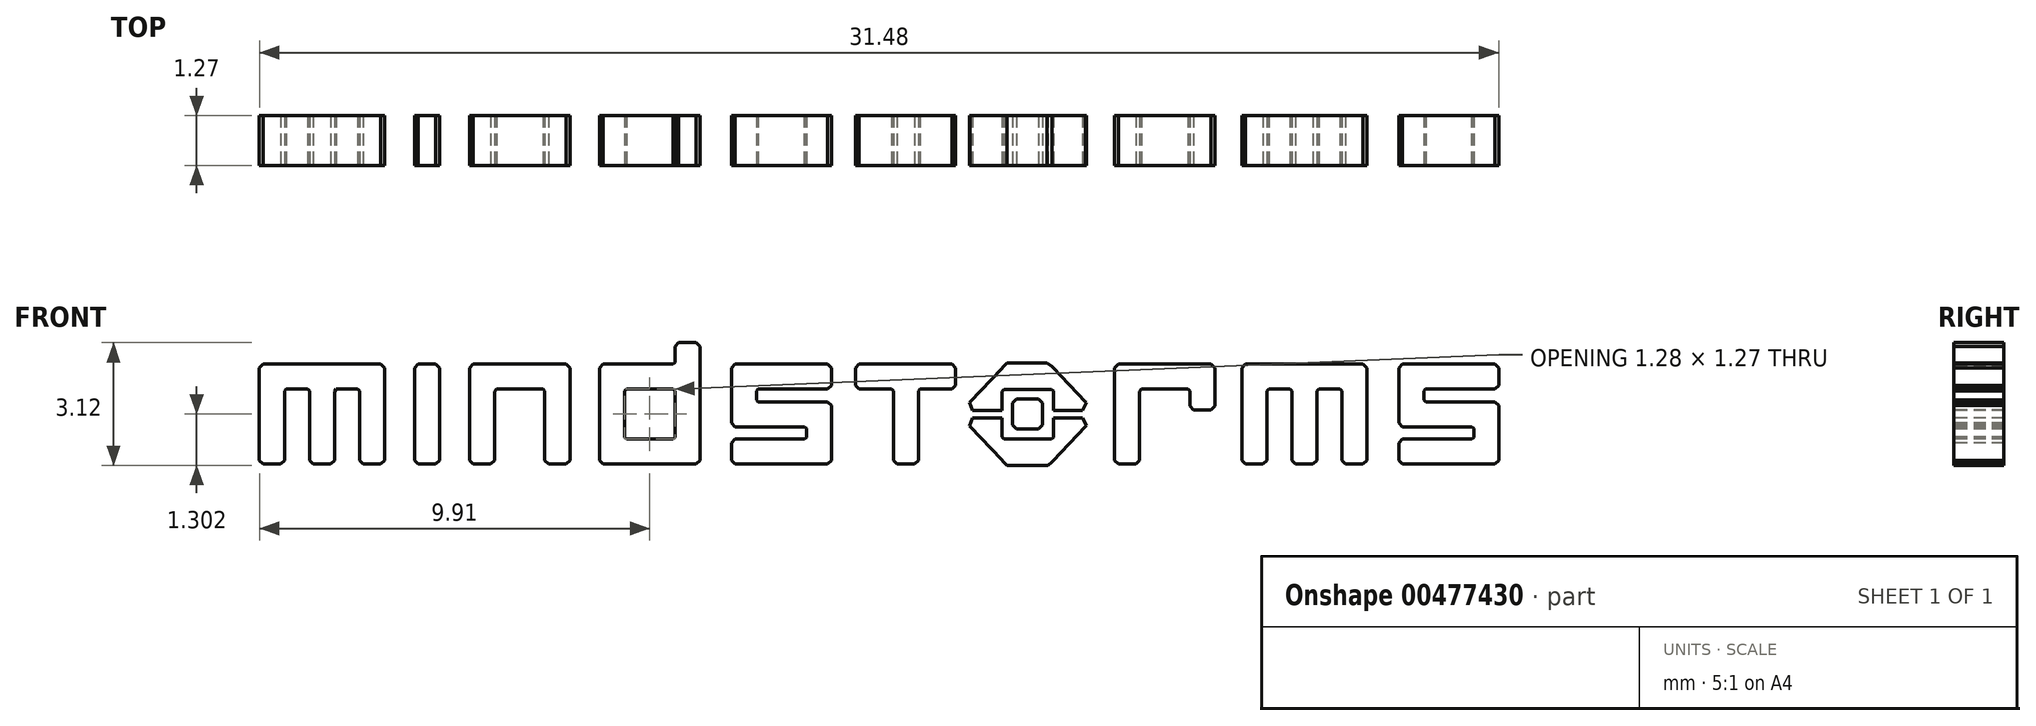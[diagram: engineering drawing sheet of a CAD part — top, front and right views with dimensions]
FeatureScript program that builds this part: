
annotation { "Feature Type Name" : "Feature", "Feature Type Description" : "" }
export const myFeature = defineFeature(function(context is Context, id is Id, definition is map)
    precondition{}
    {
        {
            var Q0;
            Q0=qCreatedBy(makeId("Front.planeOp"),FACE);
            var sketch = newSketch(context, id + "F0", { "sketchPlane" : qUnion([Q0])});
            skLineSegment(sketch, "E0", {"start": v(4.43, -0.35) * mm, "end": v(5.14, -0.35) * mm});
            skLineSegment(sketch, "E1", {"start": v(5.14, -0.35) * mm, "end": v(5.17, -0.35) * mm});
            skLineSegment(sketch, "E2", {"start": v(5.17, -0.35) * mm, "end": v(5.26, -0.55) * mm});
            skLineSegment(sketch, "E3", {"start": v(5.26, -0.55) * mm, "end": v(5.25, -0.57) * mm});
            skLineSegment(sketch, "E4", {"start": v(5.25, -0.57) * mm, "end": v(4.42, -1.44) * mm});
            skLineSegment(sketch, "E5", {"start": v(4.42, -1.44) * mm, "end": v(4.38, -1.47) * mm});
            skLineSegment(sketch, "E6", {"start": v(4.38, -1.47) * mm, "end": v(4.29, -1.56) * mm});
            skLineSegment(sketch, "E7", {"start": v(4.29, -1.56) * mm, "end": v(4.25, -1.56) * mm});
            skLineSegment(sketch, "E8", {"start": v(4.25, -1.56) * mm, "end": v(3.3, -1.56) * mm});
            skLineSegment(sketch, "E9", {"start": v(3.3, -1.56) * mm, "end": v(3.25, -1.56) * mm});
            skLineSegment(sketch, "E10", {"start": v(3.25, -1.56) * mm, "end": v(3.15, -1.46) * mm});
            skLineSegment(sketch, "E11", {"start": v(3.15, -1.46) * mm, "end": v(3.11, -1.42) * mm});
            skLineSegment(sketch, "E12", {"start": v(3.11, -1.42) * mm, "end": v(2.3, -0.57) * mm});
            skLineSegment(sketch, "E13", {"start": v(2.3, -0.57) * mm, "end": v(2.3, -0.55) * mm});
            skLineSegment(sketch, "E14", {"start": v(2.3, -0.55) * mm, "end": v(2.38, -0.35) * mm});
            skLineSegment(sketch, "E15", {"start": v(2.38, -0.35) * mm, "end": v(2.4, -0.35) * mm});
            skLineSegment(sketch, "E16", {"start": v(2.4, -0.35) * mm, "end": v(3.12, -0.35) * mm});
            skLineSegment(sketch, "E17", {"start": v(3.12, -0.35) * mm, "end": v(3.12, -0.83) * mm});
            skLineSegment(sketch, "E18", {"start": v(3.12, -0.83) * mm, "end": v(3.12, -0.84) * mm});
            skLineSegment(sketch, "E19", {"start": v(3.12, -0.84) * mm, "end": v(3.17, -0.9) * mm});
            skLineSegment(sketch, "E20", {"start": v(3.17, -0.9) * mm, "end": v(3.18, -0.9) * mm});
            skLineSegment(sketch, "E21", {"start": v(3.18, -0.9) * mm, "end": v(4.36, -0.9) * mm});
            skLineSegment(sketch, "E22", {"start": v(4.36, -0.9) * mm, "end": v(4.38, -0.9) * mm});
            skLineSegment(sketch, "E23", {"start": v(4.38, -0.9) * mm, "end": v(4.43, -0.84) * mm});
            skLineSegment(sketch, "E24", {"start": v(4.43, -0.84) * mm, "end": v(4.43, -0.83) * mm});
            skLineSegment(sketch, "E25", {"start": v(4.43, -0.83) * mm, "end": v(4.43, -0.35) * mm});
            skLineSegment(sketch, "E26", {"start": v(4.43, -0.16) * mm, "end": v(5.14, -0.16) * mm});
            skLineSegment(sketch, "E27", {"start": v(5.14, -0.16) * mm, "end": v(5.17, -0.16) * mm});
            skLineSegment(sketch, "E28", {"start": v(5.17, -0.16) * mm, "end": v(5.26, 0.04) * mm});
            skLineSegment(sketch, "E29", {"start": v(5.26, 0.04) * mm, "end": v(5.25, 0.05) * mm});
            skLineSegment(sketch, "E30", {"start": v(5.25, 0.05) * mm, "end": v(4.42, 0.93) * mm});
            skLineSegment(sketch, "E31", {"start": v(4.42, 0.93) * mm, "end": v(4.39, 0.96) * mm});
            skLineSegment(sketch, "E32", {"start": v(4.39, 0.96) * mm, "end": v(4.26, 1.05) * mm});
            skLineSegment(sketch, "E33", {"start": v(4.26, 1.05) * mm, "end": v(4.25, 1.05) * mm});
            skLineSegment(sketch, "E34", {"start": v(4.25, 1.05) * mm, "end": v(3.3, 1.05) * mm});
            skLineSegment(sketch, "E35", {"start": v(3.3, 1.05) * mm, "end": v(3.25, 1.05) * mm});
            skLineSegment(sketch, "E36", {"start": v(3.25, 1.05) * mm, "end": v(3.15, 0.94) * mm});
            skLineSegment(sketch, "E37", {"start": v(3.15, 0.94) * mm, "end": v(3.11, 0.9) * mm});
            skLineSegment(sketch, "E38", {"start": v(3.11, 0.9) * mm, "end": v(2.3, 0.05) * mm});
            skLineSegment(sketch, "E39", {"start": v(2.3, 0.05) * mm, "end": v(2.3, 0.04) * mm});
            skLineSegment(sketch, "E40", {"start": v(2.3, 0.04) * mm, "end": v(2.38, -0.16) * mm});
            skLineSegment(sketch, "E41", {"start": v(2.38, -0.16) * mm, "end": v(2.4, -0.16) * mm});
            skLineSegment(sketch, "E42", {"start": v(2.4, -0.16) * mm, "end": v(3.12, -0.16) * mm});
            skLineSegment(sketch, "E43", {"start": v(3.12, -0.16) * mm, "end": v(3.12, 0.31) * mm});
            skLineSegment(sketch, "E44", {"start": v(3.12, 0.31) * mm, "end": v(3.12, 0.32) * mm});
            skLineSegment(sketch, "E45", {"start": v(3.12, 0.32) * mm, "end": v(3.17, 0.38) * mm});
            skLineSegment(sketch, "E46", {"start": v(3.17, 0.38) * mm, "end": v(3.19, 0.38) * mm});
            skLineSegment(sketch, "E47", {"start": v(3.19, 0.38) * mm, "end": v(4.36, 0.38) * mm});
            skLineSegment(sketch, "E48", {"start": v(4.36, 0.38) * mm, "end": v(4.38, 0.38) * mm});
            skLineSegment(sketch, "E49", {"start": v(4.38, 0.38) * mm, "end": v(4.43, 0.33) * mm});
            skLineSegment(sketch, "E50", {"start": v(4.43, 0.33) * mm, "end": v(4.43, 0.31) * mm});
            skLineSegment(sketch, "E51", {"start": v(4.43, 0.31) * mm, "end": v(4.43, -0.16) * mm});
            skLineSegment(sketch, "E52", {"start": v(8.4, 1.01) * mm, "end": v(6.1, 1.01) * mm});
            skLineSegment(sketch, "E53", {"start": v(6.1, 1.01) * mm, "end": v(6.08, 1.01) * mm});
            skLineSegment(sketch, "E54", {"start": v(6.08, 1.01) * mm, "end": v(5.98, 0.92) * mm});
            skLineSegment(sketch, "E55", {"start": v(5.98, 0.92) * mm, "end": v(5.98, 0.89) * mm});
            skLineSegment(sketch, "E56", {"start": v(5.98, 0.89) * mm, "end": v(5.98, -1.4) * mm});
            skLineSegment(sketch, "E57", {"start": v(5.98, -1.4) * mm, "end": v(5.98, -1.43) * mm});
            skLineSegment(sketch, "E58", {"start": v(5.98, -1.43) * mm, "end": v(6.08, -1.53) * mm});
            skLineSegment(sketch, "E59", {"start": v(6.08, -1.53) * mm, "end": v(6.1, -1.53) * mm});
            skLineSegment(sketch, "E60", {"start": v(6.1, -1.53) * mm, "end": v(6.49, -1.53) * mm});
            skLineSegment(sketch, "E61", {"start": v(6.49, -1.53) * mm, "end": v(6.52, -1.53) * mm});
            skLineSegment(sketch, "E62", {"start": v(6.52, -1.53) * mm, "end": v(6.62, -1.43) * mm});
            skLineSegment(sketch, "E63", {"start": v(6.62, -1.43) * mm, "end": v(6.62, -1.4) * mm});
            skLineSegment(sketch, "E64", {"start": v(6.62, -1.4) * mm, "end": v(6.62, 0.32) * mm});
            skLineSegment(sketch, "E65", {"start": v(6.62, 0.32) * mm, "end": v(6.62, 0.32) * mm});
            skLineSegment(sketch, "E66", {"start": v(6.62, 0.32) * mm, "end": v(6.66, 0.38) * mm});
            skLineSegment(sketch, "E67", {"start": v(6.66, 0.38) * mm, "end": v(6.68, 0.38) * mm});
            skLineSegment(sketch, "E68", {"start": v(6.68, 0.38) * mm, "end": v(7.83, 0.38) * mm});
            skLineSegment(sketch, "E69", {"start": v(7.83, 0.38) * mm, "end": v(7.84, 0.38) * mm});
            skLineSegment(sketch, "E70", {"start": v(7.84, 0.38) * mm, "end": v(7.9, 0.33) * mm});
            skLineSegment(sketch, "E71", {"start": v(7.9, 0.33) * mm, "end": v(7.9, 0.32) * mm});
            skLineSegment(sketch, "E72", {"start": v(7.9, 0.32) * mm, "end": v(7.9, -0.02) * mm});
            skLineSegment(sketch, "E73", {"start": v(7.9, -0.02) * mm, "end": v(7.9, -0.05) * mm});
            skLineSegment(sketch, "E74", {"start": v(7.9, -0.05) * mm, "end": v(7.99, -0.15) * mm});
            skLineSegment(sketch, "E75", {"start": v(7.99, -0.15) * mm, "end": v(8.02, -0.15) * mm});
            skLineSegment(sketch, "E76", {"start": v(8.02, -0.15) * mm, "end": v(8.4, -0.15) * mm});
            skLineSegment(sketch, "E77", {"start": v(8.4, -0.15) * mm, "end": v(8.43, -0.15) * mm});
            skLineSegment(sketch, "E78", {"start": v(8.43, -0.15) * mm, "end": v(8.53, -0.05) * mm});
            skLineSegment(sketch, "E79", {"start": v(8.53, -0.05) * mm, "end": v(8.53, -0.02) * mm});
            skLineSegment(sketch, "E80", {"start": v(8.53, -0.02) * mm, "end": v(8.53, 0.89) * mm});
            skLineSegment(sketch, "E81", {"start": v(8.53, 0.89) * mm, "end": v(8.53, 0.92) * mm});
            skLineSegment(sketch, "E82", {"start": v(8.53, 0.92) * mm, "end": v(8.43, 1.01) * mm});
            skLineSegment(sketch, "E83", {"start": v(8.43, 1.01) * mm, "end": v(8.4, 1.01) * mm});
            skLineSegment(sketch, "E84", {"start": v(13.84, 0.32) * mm, "end": v(13.84, 0.33) * mm});
            skLineSegment(sketch, "E85", {"start": v(13.84, 0.33) * mm, "end": v(13.88, 0.38) * mm});
            skLineSegment(sketch, "E86", {"start": v(13.88, 0.38) * mm, "end": v(13.9, 0.38) * mm});
            skLineSegment(sketch, "E87", {"start": v(13.9, 0.38) * mm, "end": v(15.62, 0.38) * mm});
            skLineSegment(sketch, "E88", {"start": v(15.62, 0.38) * mm, "end": v(15.65, 0.38) * mm});
            skLineSegment(sketch, "E89", {"start": v(15.65, 0.38) * mm, "end": v(15.74, 0.47) * mm});
            skLineSegment(sketch, "E90", {"start": v(15.74, 0.47) * mm, "end": v(15.74, 0.5) * mm});
            skLineSegment(sketch, "E91", {"start": v(15.74, 0.5) * mm, "end": v(15.74, 0.89) * mm});
            skLineSegment(sketch, "E92", {"start": v(15.74, 0.89) * mm, "end": v(15.74, 0.92) * mm});
            skLineSegment(sketch, "E93", {"start": v(15.74, 0.92) * mm, "end": v(15.65, 1.01) * mm});
            skLineSegment(sketch, "E94", {"start": v(15.65, 1.01) * mm, "end": v(15.62, 1.01) * mm});
            skLineSegment(sketch, "E95", {"start": v(15.62, 1.01) * mm, "end": v(13.33, 1.01) * mm});
            skLineSegment(sketch, "E96", {"start": v(13.33, 1.01) * mm, "end": v(13.3, 1.01) * mm});
            skLineSegment(sketch, "E97", {"start": v(13.3, 1.01) * mm, "end": v(13.2, 0.92) * mm});
            skLineSegment(sketch, "E98", {"start": v(13.2, 0.92) * mm, "end": v(13.2, 0.89) * mm});
            skLineSegment(sketch, "E99", {"start": v(13.2, 0.89) * mm, "end": v(13.2, -0.45) * mm});
            skLineSegment(sketch, "E100", {"start": v(13.2, -0.45) * mm, "end": v(13.2, -0.48) * mm});
            skLineSegment(sketch, "E101", {"start": v(13.2, -0.48) * mm, "end": v(13.3, -0.58) * mm});
            skLineSegment(sketch, "E102", {"start": v(13.3, -0.58) * mm, "end": v(13.33, -0.58) * mm});
            skLineSegment(sketch, "E103", {"start": v(13.33, -0.58) * mm, "end": v(15.05, -0.58) * mm});
            skLineSegment(sketch, "E104", {"start": v(15.05, -0.58) * mm, "end": v(15.06, -0.58) * mm});
            skLineSegment(sketch, "E105", {"start": v(15.06, -0.58) * mm, "end": v(15.1, -0.62) * mm});
            skLineSegment(sketch, "E106", {"start": v(15.1, -0.62) * mm, "end": v(15.1, -0.64) * mm});
            skLineSegment(sketch, "E107", {"start": v(15.1, -0.64) * mm, "end": v(15.1, -0.83) * mm});
            skLineSegment(sketch, "E108", {"start": v(15.1, -0.83) * mm, "end": v(15.1, -0.85) * mm});
            skLineSegment(sketch, "E109", {"start": v(15.1, -0.85) * mm, "end": v(15.06, -0.9) * mm});
            skLineSegment(sketch, "E110", {"start": v(15.06, -0.9) * mm, "end": v(15.05, -0.9) * mm});
            skLineSegment(sketch, "E111", {"start": v(15.05, -0.9) * mm, "end": v(13.33, -0.9) * mm});
            skLineSegment(sketch, "E112", {"start": v(13.33, -0.9) * mm, "end": v(13.3, -0.9) * mm});
            skLineSegment(sketch, "E113", {"start": v(13.3, -0.9) * mm, "end": v(13.2, -1) * mm});
            skLineSegment(sketch, "E114", {"start": v(13.2, -1) * mm, "end": v(13.2, -1.02) * mm});
            skLineSegment(sketch, "E115", {"start": v(13.2, -1.02) * mm, "end": v(13.2, -1.4) * mm});
            skLineSegment(sketch, "E116", {"start": v(13.2, -1.4) * mm, "end": v(13.2, -1.43) * mm});
            skLineSegment(sketch, "E117", {"start": v(13.2, -1.43) * mm, "end": v(13.3, -1.53) * mm});
            skLineSegment(sketch, "E118", {"start": v(13.3, -1.53) * mm, "end": v(13.33, -1.53) * mm});
            skLineSegment(sketch, "E119", {"start": v(13.33, -1.53) * mm, "end": v(15.62, -1.53) * mm});
            skLineSegment(sketch, "E120", {"start": v(15.62, -1.53) * mm, "end": v(15.65, -1.53) * mm});
            skLineSegment(sketch, "E121", {"start": v(15.65, -1.53) * mm, "end": v(15.74, -1.43) * mm});
            skLineSegment(sketch, "E122", {"start": v(15.74, -1.43) * mm, "end": v(15.74, -1.4) * mm});
            skLineSegment(sketch, "E123", {"start": v(15.74, -1.4) * mm, "end": v(15.74, -0.07) * mm});
            skLineSegment(sketch, "E124", {"start": v(15.74, -0.07) * mm, "end": v(15.74, -0.04) * mm});
            skLineSegment(sketch, "E125", {"start": v(15.74, -0.04) * mm, "end": v(15.65, 0.06) * mm});
            skLineSegment(sketch, "E126", {"start": v(15.65, 0.06) * mm, "end": v(15.62, 0.06) * mm});
            skLineSegment(sketch, "E127", {"start": v(15.62, 0.06) * mm, "end": v(13.9, 0.06) * mm});
            skLineSegment(sketch, "E128", {"start": v(13.9, 0.06) * mm, "end": v(13.88, 0.06) * mm});
            skLineSegment(sketch, "E129", {"start": v(13.88, 0.06) * mm, "end": v(13.84, 0.1) * mm});
            skLineSegment(sketch, "E130", {"start": v(13.84, 0.1) * mm, "end": v(13.84, 0.12) * mm});
            skLineSegment(sketch, "E131", {"start": v(13.84, 0.12) * mm, "end": v(13.84, 0.32) * mm});
            skLineSegment(sketch, "E132", {"start": v(-3.12, 0.32) * mm, "end": v(-3.12, 0.33) * mm});
            skLineSegment(sketch, "E133", {"start": v(-3.12, 0.33) * mm, "end": v(-3.08, 0.38) * mm});
            skLineSegment(sketch, "E134", {"start": v(-3.08, 0.38) * mm, "end": v(-3.06, 0.38) * mm});
            skLineSegment(sketch, "E135", {"start": v(-3.06, 0.38) * mm, "end": v(-1.34, 0.38) * mm});
            skLineSegment(sketch, "E136", {"start": v(-1.34, 0.38) * mm, "end": v(-1.31, 0.38) * mm});
            skLineSegment(sketch, "E137", {"start": v(-1.31, 0.38) * mm, "end": v(-1.21, 0.47) * mm});
            skLineSegment(sketch, "E138", {"start": v(-1.21, 0.47) * mm, "end": v(-1.21, 0.5) * mm});
            skLineSegment(sketch, "E139", {"start": v(-1.21, 0.5) * mm, "end": v(-1.21, 0.89) * mm});
            skLineSegment(sketch, "E140", {"start": v(-1.21, 0.89) * mm, "end": v(-1.21, 0.92) * mm});
            skLineSegment(sketch, "E141", {"start": v(-1.21, 0.92) * mm, "end": v(-1.31, 1.01) * mm});
            skLineSegment(sketch, "E142", {"start": v(-1.31, 1.01) * mm, "end": v(-1.34, 1.01) * mm});
            skLineSegment(sketch, "E143", {"start": v(-1.34, 1.01) * mm, "end": v(-3.63, 1.01) * mm});
            skLineSegment(sketch, "E144", {"start": v(-3.63, 1.01) * mm, "end": v(-3.66, 1.01) * mm});
            skLineSegment(sketch, "E145", {"start": v(-3.66, 1.01) * mm, "end": v(-3.76, 0.92) * mm});
            skLineSegment(sketch, "E146", {"start": v(-3.76, 0.92) * mm, "end": v(-3.76, 0.89) * mm});
            skLineSegment(sketch, "E147", {"start": v(-3.76, 0.89) * mm, "end": v(-3.76, -0.45) * mm});
            skLineSegment(sketch, "E148", {"start": v(-3.76, -0.45) * mm, "end": v(-3.76, -0.48) * mm});
            skLineSegment(sketch, "E149", {"start": v(-3.76, -0.48) * mm, "end": v(-3.66, -0.58) * mm});
            skLineSegment(sketch, "E150", {"start": v(-3.66, -0.58) * mm, "end": v(-3.63, -0.58) * mm});
            skLineSegment(sketch, "E151", {"start": v(-3.63, -0.58) * mm, "end": v(-1.9, -0.58) * mm});
            skLineSegment(sketch, "E152", {"start": v(-1.9, -0.58) * mm, "end": v(-1.9, -0.58) * mm});
            skLineSegment(sketch, "E153", {"start": v(-1.9, -0.58) * mm, "end": v(-1.85, -0.62) * mm});
            skLineSegment(sketch, "E154", {"start": v(-1.85, -0.62) * mm, "end": v(-1.85, -0.64) * mm});
            skLineSegment(sketch, "E155", {"start": v(-1.85, -0.64) * mm, "end": v(-1.85, -0.83) * mm});
            skLineSegment(sketch, "E156", {"start": v(-1.85, -0.83) * mm, "end": v(-1.85, -0.85) * mm});
            skLineSegment(sketch, "E157", {"start": v(-1.85, -0.85) * mm, "end": v(-1.9, -0.9) * mm});
            skLineSegment(sketch, "E158", {"start": v(-1.9, -0.9) * mm, "end": v(-1.9, -0.9) * mm});
            skLineSegment(sketch, "E159", {"start": v(-1.9, -0.9) * mm, "end": v(-3.63, -0.9) * mm});
            skLineSegment(sketch, "E160", {"start": v(-3.63, -0.9) * mm, "end": v(-3.66, -0.9) * mm});
            skLineSegment(sketch, "E161", {"start": v(-3.66, -0.9) * mm, "end": v(-3.76, -1) * mm});
            skLineSegment(sketch, "E162", {"start": v(-3.76, -1) * mm, "end": v(-3.76, -1.02) * mm});
            skLineSegment(sketch, "E163", {"start": v(-3.76, -1.02) * mm, "end": v(-3.76, -1.4) * mm});
            skLineSegment(sketch, "E164", {"start": v(-3.76, -1.4) * mm, "end": v(-3.76, -1.43) * mm});
            skLineSegment(sketch, "E165", {"start": v(-3.76, -1.43) * mm, "end": v(-3.66, -1.53) * mm});
            skLineSegment(sketch, "E166", {"start": v(-3.66, -1.53) * mm, "end": v(-3.63, -1.53) * mm});
            skLineSegment(sketch, "E167", {"start": v(-3.63, -1.53) * mm, "end": v(-1.34, -1.53) * mm});
            skLineSegment(sketch, "E168", {"start": v(-1.34, -1.53) * mm, "end": v(-1.31, -1.53) * mm});
            skLineSegment(sketch, "E169", {"start": v(-1.31, -1.53) * mm, "end": v(-1.21, -1.43) * mm});
            skLineSegment(sketch, "E170", {"start": v(-1.21, -1.43) * mm, "end": v(-1.21, -1.4) * mm});
            skLineSegment(sketch, "E171", {"start": v(-1.21, -1.4) * mm, "end": v(-1.21, -0.07) * mm});
            skLineSegment(sketch, "E172", {"start": v(-1.21, -0.07) * mm, "end": v(-1.21, -0.04) * mm});
            skLineSegment(sketch, "E173", {"start": v(-1.21, -0.04) * mm, "end": v(-1.31, 0.06) * mm});
            skLineSegment(sketch, "E174", {"start": v(-1.31, 0.06) * mm, "end": v(-1.34, 0.06) * mm});
            skLineSegment(sketch, "E175", {"start": v(-1.34, 0.06) * mm, "end": v(-3.06, 0.06) * mm});
            skLineSegment(sketch, "E176", {"start": v(-3.06, 0.06) * mm, "end": v(-3.07, 0.06) * mm});
            skLineSegment(sketch, "E177", {"start": v(-3.07, 0.06) * mm, "end": v(-3.12, 0.1) * mm});
            skLineSegment(sketch, "E178", {"start": v(-3.12, 0.1) * mm, "end": v(-3.12, 0.12) * mm});
            skLineSegment(sketch, "E179", {"start": v(-3.12, 0.12) * mm, "end": v(-3.12, 0.32) * mm});
            skLineSegment(sketch, "E180", {"start": v(-5.2, -0.83) * mm, "end": v(-5.2, -0.85) * mm});
            skLineSegment(sketch, "E181", {"start": v(-5.2, -0.85) * mm, "end": v(-5.24, -0.9) * mm});
            skLineSegment(sketch, "E182", {"start": v(-5.24, -0.9) * mm, "end": v(-5.25, -0.9) * mm});
            skLineSegment(sketch, "E183", {"start": v(-5.25, -0.9) * mm, "end": v(-6.4, -0.9) * mm});
            skLineSegment(sketch, "E184", {"start": v(-6.4, -0.9) * mm, "end": v(-6.42, -0.9) * mm});
            skLineSegment(sketch, "E185", {"start": v(-6.42, -0.9) * mm, "end": v(-6.47, -0.85) * mm});
            skLineSegment(sketch, "E186", {"start": v(-6.47, -0.85) * mm, "end": v(-6.47, -0.83) * mm});
            skLineSegment(sketch, "E187", {"start": v(-6.47, -0.83) * mm, "end": v(-6.47, 0.32) * mm});
            skLineSegment(sketch, "E188", {"start": v(-6.47, 0.32) * mm, "end": v(-6.47, 0.33) * mm});
            skLineSegment(sketch, "E189", {"start": v(-6.47, 0.33) * mm, "end": v(-6.42, 0.38) * mm});
            skLineSegment(sketch, "E190", {"start": v(-6.42, 0.38) * mm, "end": v(-6.4, 0.38) * mm});
            skLineSegment(sketch, "E191", {"start": v(-6.4, 0.38) * mm, "end": v(-5.25, 0.38) * mm});
            skLineSegment(sketch, "E192", {"start": v(-5.25, 0.38) * mm, "end": v(-5.24, 0.38) * mm});
            skLineSegment(sketch, "E193", {"start": v(-5.24, 0.38) * mm, "end": v(-5.2, 0.33) * mm});
            skLineSegment(sketch, "E194", {"start": v(-5.2, 0.33) * mm, "end": v(-5.2, 0.32) * mm});
            skLineSegment(sketch, "E195", {"start": v(-5.2, 0.32) * mm, "end": v(-5.2, -0.83) * mm});
            skLineSegment(sketch, "E196", {"start": v(-4.68, 1.56) * mm, "end": v(-5.06, 1.56) * mm});
            skLineSegment(sketch, "E197", {"start": v(-5.06, 1.56) * mm, "end": v(-5.1, 1.56) * mm});
            skLineSegment(sketch, "E198", {"start": v(-5.1, 1.56) * mm, "end": v(-5.2, 1.47) * mm});
            skLineSegment(sketch, "E199", {"start": v(-5.2, 1.47) * mm, "end": v(-5.2, 1.43) * mm});
            skLineSegment(sketch, "E200", {"start": v(-5.2, 1.43) * mm, "end": v(-5.2, 1.08) * mm});
            skLineSegment(sketch, "E201", {"start": v(-5.2, 1.08) * mm, "end": v(-5.2, 1.06) * mm});
            skLineSegment(sketch, "E202", {"start": v(-5.2, 1.06) * mm, "end": v(-5.24, 1.01) * mm});
            skLineSegment(sketch, "E203", {"start": v(-5.24, 1.01) * mm, "end": v(-5.25, 1.01) * mm});
            skLineSegment(sketch, "E204", {"start": v(-5.25, 1.01) * mm, "end": v(-6.98, 1.01) * mm});
            skLineSegment(sketch, "E205", {"start": v(-6.98, 1.01) * mm, "end": v(-7.01, 1.01) * mm});
            skLineSegment(sketch, "E206", {"start": v(-7.01, 1.01) * mm, "end": v(-7.1, 0.92) * mm});
            skLineSegment(sketch, "E207", {"start": v(-7.1, 0.92) * mm, "end": v(-7.1, 0.89) * mm});
            skLineSegment(sketch, "E208", {"start": v(-7.1, 0.89) * mm, "end": v(-7.1, -1.4) * mm});
            skLineSegment(sketch, "E209", {"start": v(-7.1, -1.4) * mm, "end": v(-7.1, -1.43) * mm});
            skLineSegment(sketch, "E210", {"start": v(-7.1, -1.43) * mm, "end": v(-7.01, -1.53) * mm});
            skLineSegment(sketch, "E211", {"start": v(-7.01, -1.53) * mm, "end": v(-6.98, -1.53) * mm});
            skLineSegment(sketch, "E212", {"start": v(-6.98, -1.53) * mm, "end": v(-4.68, -1.53) * mm});
            skLineSegment(sketch, "E213", {"start": v(-4.68, -1.53) * mm, "end": v(-4.65, -1.53) * mm});
            skLineSegment(sketch, "E214", {"start": v(-4.65, -1.53) * mm, "end": v(-4.56, -1.43) * mm});
            skLineSegment(sketch, "E215", {"start": v(-4.56, -1.43) * mm, "end": v(-4.56, -1.4) * mm});
            skLineSegment(sketch, "E216", {"start": v(-4.56, -1.4) * mm, "end": v(-4.56, 1.43) * mm});
            skLineSegment(sketch, "E217", {"start": v(-4.56, 1.43) * mm, "end": v(-4.56, 1.47) * mm});
            skLineSegment(sketch, "E218", {"start": v(-4.56, 1.47) * mm, "end": v(-4.65, 1.56) * mm});
            skLineSegment(sketch, "E219", {"start": v(-4.65, 1.56) * mm, "end": v(-4.68, 1.56) * mm});
            skLineSegment(sketch, "E220", {"start": v(1.81, 1.01) * mm, "end": v(-0.47, 1.01) * mm});
            skLineSegment(sketch, "E221", {"start": v(-0.47, 1.01) * mm, "end": v(-0.5, 1.01) * mm});
            skLineSegment(sketch, "E222", {"start": v(-0.5, 1.01) * mm, "end": v(-0.6, 0.92) * mm});
            skLineSegment(sketch, "E223", {"start": v(-0.6, 0.92) * mm, "end": v(-0.6, 0.89) * mm});
            skLineSegment(sketch, "E224", {"start": v(-0.6, 0.89) * mm, "end": v(-0.6, 0.5) * mm});
            skLineSegment(sketch, "E225", {"start": v(-0.6, 0.5) * mm, "end": v(-0.6, 0.47) * mm});
            skLineSegment(sketch, "E226", {"start": v(-0.6, 0.47) * mm, "end": v(-0.5, 0.38) * mm});
            skLineSegment(sketch, "E227", {"start": v(-0.5, 0.38) * mm, "end": v(-0.47, 0.38) * mm});
            skLineSegment(sketch, "E228", {"start": v(-0.47, 0.38) * mm, "end": v(0.3, 0.38) * mm});
            skLineSegment(sketch, "E229", {"start": v(0.3, 0.38) * mm, "end": v(0.31, 0.38) * mm});
            skLineSegment(sketch, "E230", {"start": v(0.31, 0.38) * mm, "end": v(0.36, 0.33) * mm});
            skLineSegment(sketch, "E231", {"start": v(0.36, 0.33) * mm, "end": v(0.36, 0.32) * mm});
            skLineSegment(sketch, "E232", {"start": v(0.36, 0.32) * mm, "end": v(0.36, -1.4) * mm});
            skLineSegment(sketch, "E233", {"start": v(0.36, -1.4) * mm, "end": v(0.36, -1.43) * mm});
            skLineSegment(sketch, "E234", {"start": v(0.36, -1.43) * mm, "end": v(0.45, -1.53) * mm});
            skLineSegment(sketch, "E235", {"start": v(0.45, -1.53) * mm, "end": v(0.49, -1.53) * mm});
            skLineSegment(sketch, "E236", {"start": v(0.49, -1.53) * mm, "end": v(0.87, -1.53) * mm});
            skLineSegment(sketch, "E237", {"start": v(0.87, -1.53) * mm, "end": v(0.9, -1.53) * mm});
            skLineSegment(sketch, "E238", {"start": v(0.9, -1.53) * mm, "end": v(1, -1.43) * mm});
            skLineSegment(sketch, "E239", {"start": v(1, -1.43) * mm, "end": v(1, -1.4) * mm});
            skLineSegment(sketch, "E240", {"start": v(1, -1.4) * mm, "end": v(1, 0.32) * mm});
            skLineSegment(sketch, "E241", {"start": v(1, 0.32) * mm, "end": v(1, 0.33) * mm});
            skLineSegment(sketch, "E242", {"start": v(1, 0.33) * mm, "end": v(1.04, 0.38) * mm});
            skLineSegment(sketch, "E243", {"start": v(1.04, 0.38) * mm, "end": v(1.06, 0.38) * mm});
            skLineSegment(sketch, "E244", {"start": v(1.06, 0.38) * mm, "end": v(1.81, 0.38) * mm});
            skLineSegment(sketch, "E245", {"start": v(1.81, 0.38) * mm, "end": v(1.84, 0.38) * mm});
            skLineSegment(sketch, "E246", {"start": v(1.84, 0.38) * mm, "end": v(1.94, 0.47) * mm});
            skLineSegment(sketch, "E247", {"start": v(1.94, 0.47) * mm, "end": v(1.94, 0.5) * mm});
            skLineSegment(sketch, "E248", {"start": v(1.94, 0.5) * mm, "end": v(1.94, 0.89) * mm});
            skLineSegment(sketch, "E249", {"start": v(1.94, 0.89) * mm, "end": v(1.94, 0.92) * mm});
            skLineSegment(sketch, "E250", {"start": v(1.94, 0.92) * mm, "end": v(1.84, 1.01) * mm});
            skLineSegment(sketch, "E251", {"start": v(1.84, 1.01) * mm, "end": v(1.81, 1.01) * mm});
            skLineSegment(sketch, "E252", {"start": v(-7.98, 1.01) * mm, "end": v(-10.28, 1.01) * mm});
            skLineSegment(sketch, "E253", {"start": v(-10.28, 1.01) * mm, "end": v(-10.31, 1.01) * mm});
            skLineSegment(sketch, "E254", {"start": v(-10.31, 1.01) * mm, "end": v(-10.4, 0.92) * mm});
            skLineSegment(sketch, "E255", {"start": v(-10.4, 0.92) * mm, "end": v(-10.4, 0.89) * mm});
            skLineSegment(sketch, "E256", {"start": v(-10.4, 0.89) * mm, "end": v(-10.4, -1.4) * mm});
            skLineSegment(sketch, "E257", {"start": v(-10.4, -1.4) * mm, "end": v(-10.4, -1.43) * mm});
            skLineSegment(sketch, "E258", {"start": v(-10.4, -1.43) * mm, "end": v(-10.31, -1.53) * mm});
            skLineSegment(sketch, "E259", {"start": v(-10.31, -1.53) * mm, "end": v(-10.28, -1.53) * mm});
            skLineSegment(sketch, "E260", {"start": v(-10.28, -1.53) * mm, "end": v(-9.9, -1.53) * mm});
            skLineSegment(sketch, "E261", {"start": v(-9.9, -1.53) * mm, "end": v(-9.87, -1.53) * mm});
            skLineSegment(sketch, "E262", {"start": v(-9.87, -1.53) * mm, "end": v(-9.77, -1.43) * mm});
            skLineSegment(sketch, "E263", {"start": v(-9.77, -1.43) * mm, "end": v(-9.77, -1.4) * mm});
            skLineSegment(sketch, "E264", {"start": v(-9.77, -1.4) * mm, "end": v(-9.77, 0.32) * mm});
            skLineSegment(sketch, "E265", {"start": v(-9.77, 0.32) * mm, "end": v(-9.77, 0.32) * mm});
            skLineSegment(sketch, "E266", {"start": v(-9.77, 0.32) * mm, "end": v(-9.72, 0.38) * mm});
            skLineSegment(sketch, "E267", {"start": v(-9.72, 0.38) * mm, "end": v(-9.7, 0.38) * mm});
            skLineSegment(sketch, "E268", {"start": v(-9.7, 0.38) * mm, "end": v(-8.56, 0.38) * mm});
            skLineSegment(sketch, "E269", {"start": v(-8.56, 0.38) * mm, "end": v(-8.54, 0.38) * mm});
            skLineSegment(sketch, "E270", {"start": v(-8.54, 0.38) * mm, "end": v(-8.5, 0.33) * mm});
            skLineSegment(sketch, "E271", {"start": v(-8.5, 0.33) * mm, "end": v(-8.5, 0.32) * mm});
            skLineSegment(sketch, "E272", {"start": v(-8.5, 0.32) * mm, "end": v(-8.5, -1.4) * mm});
            skLineSegment(sketch, "E273", {"start": v(-8.5, -1.4) * mm, "end": v(-8.5, -1.43) * mm});
            skLineSegment(sketch, "E274", {"start": v(-8.5, -1.43) * mm, "end": v(-8.4, -1.53) * mm});
            skLineSegment(sketch, "E275", {"start": v(-8.4, -1.53) * mm, "end": v(-8.37, -1.53) * mm});
            skLineSegment(sketch, "E276", {"start": v(-8.37, -1.53) * mm, "end": v(-7.98, -1.53) * mm});
            skLineSegment(sketch, "E277", {"start": v(-7.98, -1.53) * mm, "end": v(-7.95, -1.53) * mm});
            skLineSegment(sketch, "E278", {"start": v(-7.95, -1.53) * mm, "end": v(-7.86, -1.43) * mm});
            skLineSegment(sketch, "E279", {"start": v(-7.86, -1.43) * mm, "end": v(-7.86, -1.4) * mm});
            skLineSegment(sketch, "E280", {"start": v(-7.86, -1.4) * mm, "end": v(-7.86, 0.89) * mm});
            skLineSegment(sketch, "E281", {"start": v(-7.86, 0.89) * mm, "end": v(-7.86, 0.92) * mm});
            skLineSegment(sketch, "E282", {"start": v(-7.86, 0.92) * mm, "end": v(-7.95, 1.01) * mm});
            skLineSegment(sketch, "E283", {"start": v(-7.95, 1.01) * mm, "end": v(-7.98, 1.01) * mm});
            skLineSegment(sketch, "E284", {"start": v(12.26, 1.01) * mm, "end": v(9.34, 1.01) * mm});
            skLineSegment(sketch, "E285", {"start": v(9.34, 1.01) * mm, "end": v(9.31, 1.01) * mm});
            skLineSegment(sketch, "E286", {"start": v(9.31, 1.01) * mm, "end": v(9.21, 0.92) * mm});
            skLineSegment(sketch, "E287", {"start": v(9.21, 0.92) * mm, "end": v(9.21, 0.89) * mm});
            skLineSegment(sketch, "E288", {"start": v(9.21, 0.89) * mm, "end": v(9.21, -1.4) * mm});
            skLineSegment(sketch, "E289", {"start": v(9.21, -1.4) * mm, "end": v(9.21, -1.43) * mm});
            skLineSegment(sketch, "E290", {"start": v(9.21, -1.43) * mm, "end": v(9.31, -1.53) * mm});
            skLineSegment(sketch, "E291", {"start": v(9.31, -1.53) * mm, "end": v(9.34, -1.53) * mm});
            skLineSegment(sketch, "E292", {"start": v(9.34, -1.53) * mm, "end": v(9.72, -1.53) * mm});
            skLineSegment(sketch, "E293", {"start": v(9.72, -1.53) * mm, "end": v(9.75, -1.53) * mm});
            skLineSegment(sketch, "E294", {"start": v(9.75, -1.53) * mm, "end": v(9.85, -1.43) * mm});
            skLineSegment(sketch, "E295", {"start": v(9.85, -1.43) * mm, "end": v(9.85, -1.4) * mm});
            skLineSegment(sketch, "E296", {"start": v(9.85, -1.4) * mm, "end": v(9.85, 0.32) * mm});
            skLineSegment(sketch, "E297", {"start": v(9.85, 0.32) * mm, "end": v(9.85, 0.33) * mm});
            skLineSegment(sketch, "E298", {"start": v(9.85, 0.33) * mm, "end": v(9.9, 0.38) * mm});
            skLineSegment(sketch, "E299", {"start": v(9.9, 0.38) * mm, "end": v(9.91, 0.38) * mm});
            skLineSegment(sketch, "E300", {"start": v(9.91, 0.38) * mm, "end": v(10.42, 0.38) * mm});
            skLineSegment(sketch, "E301", {"start": v(10.42, 0.38) * mm, "end": v(10.44, 0.38) * mm});
            skLineSegment(sketch, "E302", {"start": v(10.44, 0.38) * mm, "end": v(10.48, 0.33) * mm});
            skLineSegment(sketch, "E303", {"start": v(10.48, 0.33) * mm, "end": v(10.48, 0.32) * mm});
            skLineSegment(sketch, "E304", {"start": v(10.48, 0.32) * mm, "end": v(10.48, -1.4) * mm});
            skLineSegment(sketch, "E305", {"start": v(10.48, -1.4) * mm, "end": v(10.48, -1.43) * mm});
            skLineSegment(sketch, "E306", {"start": v(10.48, -1.43) * mm, "end": v(10.58, -1.53) * mm});
            skLineSegment(sketch, "E307", {"start": v(10.58, -1.53) * mm, "end": v(10.61, -1.53) * mm});
            skLineSegment(sketch, "E308", {"start": v(10.61, -1.53) * mm, "end": v(11, -1.53) * mm});
            skLineSegment(sketch, "E309", {"start": v(11, -1.53) * mm, "end": v(11.02, -1.53) * mm});
            skLineSegment(sketch, "E310", {"start": v(11.02, -1.53) * mm, "end": v(11.12, -1.43) * mm});
            skLineSegment(sketch, "E311", {"start": v(11.12, -1.43) * mm, "end": v(11.12, -1.4) * mm});
            skLineSegment(sketch, "E312", {"start": v(11.12, -1.4) * mm, "end": v(11.12, 0.32) * mm});
            skLineSegment(sketch, "E313", {"start": v(11.12, 0.32) * mm, "end": v(11.12, 0.33) * mm});
            skLineSegment(sketch, "E314", {"start": v(11.12, 0.33) * mm, "end": v(11.17, 0.38) * mm});
            skLineSegment(sketch, "E315", {"start": v(11.17, 0.38) * mm, "end": v(11.18, 0.38) * mm});
            skLineSegment(sketch, "E316", {"start": v(11.18, 0.38) * mm, "end": v(11.7, 0.38) * mm});
            skLineSegment(sketch, "E317", {"start": v(11.7, 0.38) * mm, "end": v(11.7, 0.38) * mm});
            skLineSegment(sketch, "E318", {"start": v(11.7, 0.38) * mm, "end": v(11.76, 0.33) * mm});
            skLineSegment(sketch, "E319", {"start": v(11.76, 0.33) * mm, "end": v(11.76, 0.32) * mm});
            skLineSegment(sketch, "E320", {"start": v(11.76, 0.32) * mm, "end": v(11.76, -1.4) * mm});
            skLineSegment(sketch, "E321", {"start": v(11.76, -1.4) * mm, "end": v(11.76, -1.43) * mm});
            skLineSegment(sketch, "E322", {"start": v(11.76, -1.43) * mm, "end": v(11.85, -1.53) * mm});
            skLineSegment(sketch, "E323", {"start": v(11.85, -1.53) * mm, "end": v(11.88, -1.53) * mm});
            skLineSegment(sketch, "E324", {"start": v(11.88, -1.53) * mm, "end": v(12.26, -1.53) * mm});
            skLineSegment(sketch, "E325", {"start": v(12.26, -1.53) * mm, "end": v(12.3, -1.53) * mm});
            skLineSegment(sketch, "E326", {"start": v(12.3, -1.53) * mm, "end": v(12.4, -1.43) * mm});
            skLineSegment(sketch, "E327", {"start": v(12.4, -1.43) * mm, "end": v(12.4, -1.4) * mm});
            skLineSegment(sketch, "E328", {"start": v(12.4, -1.4) * mm, "end": v(12.4, 0.89) * mm});
            skLineSegment(sketch, "E329", {"start": v(12.4, 0.89) * mm, "end": v(12.4, 0.92) * mm});
            skLineSegment(sketch, "E330", {"start": v(12.4, 0.92) * mm, "end": v(12.3, 1.01) * mm});
            skLineSegment(sketch, "E331", {"start": v(12.3, 1.01) * mm, "end": v(12.26, 1.01) * mm});
            skLineSegment(sketch, "E332", {"start": v(-12.7, 1.01) * mm, "end": v(-15.62, 1.01) * mm});
            skLineSegment(sketch, "E333", {"start": v(-15.62, 1.01) * mm, "end": v(-15.65, 1.01) * mm});
            skLineSegment(sketch, "E334", {"start": v(-15.65, 1.01) * mm, "end": v(-15.74, 0.92) * mm});
            skLineSegment(sketch, "E335", {"start": v(-15.74, 0.92) * mm, "end": v(-15.74, 0.89) * mm});
            skLineSegment(sketch, "E336", {"start": v(-15.74, 0.89) * mm, "end": v(-15.74, -1.4) * mm});
            skLineSegment(sketch, "E337", {"start": v(-15.74, -1.4) * mm, "end": v(-15.74, -1.43) * mm});
            skLineSegment(sketch, "E338", {"start": v(-15.74, -1.43) * mm, "end": v(-15.65, -1.53) * mm});
            skLineSegment(sketch, "E339", {"start": v(-15.65, -1.53) * mm, "end": v(-15.62, -1.53) * mm});
            skLineSegment(sketch, "E340", {"start": v(-15.62, -1.53) * mm, "end": v(-15.24, -1.53) * mm});
            skLineSegment(sketch, "E341", {"start": v(-15.24, -1.53) * mm, "end": v(-15.2, -1.53) * mm});
            skLineSegment(sketch, "E342", {"start": v(-15.2, -1.53) * mm, "end": v(-15.1, -1.43) * mm});
            skLineSegment(sketch, "E343", {"start": v(-15.1, -1.43) * mm, "end": v(-15.1, -1.4) * mm});
            skLineSegment(sketch, "E344", {"start": v(-15.1, -1.4) * mm, "end": v(-15.1, 0.32) * mm});
            skLineSegment(sketch, "E345", {"start": v(-15.1, 0.32) * mm, "end": v(-15.1, 0.33) * mm});
            skLineSegment(sketch, "E346", {"start": v(-15.1, 0.33) * mm, "end": v(-15.06, 0.38) * mm});
            skLineSegment(sketch, "E347", {"start": v(-15.06, 0.38) * mm, "end": v(-15.04, 0.38) * mm});
            skLineSegment(sketch, "E348", {"start": v(-15.04, 0.38) * mm, "end": v(-14.54, 0.38) * mm});
            skLineSegment(sketch, "E349", {"start": v(-14.54, 0.38) * mm, "end": v(-14.52, 0.38) * mm});
            skLineSegment(sketch, "E350", {"start": v(-14.52, 0.38) * mm, "end": v(-14.47, 0.33) * mm});
            skLineSegment(sketch, "E351", {"start": v(-14.47, 0.33) * mm, "end": v(-14.47, 0.32) * mm});
            skLineSegment(sketch, "E352", {"start": v(-14.47, 0.32) * mm, "end": v(-14.47, -1.4) * mm});
            skLineSegment(sketch, "E353", {"start": v(-14.47, -1.4) * mm, "end": v(-14.47, -1.43) * mm});
            skLineSegment(sketch, "E354", {"start": v(-14.47, -1.43) * mm, "end": v(-14.38, -1.53) * mm});
            skLineSegment(sketch, "E355", {"start": v(-14.38, -1.53) * mm, "end": v(-14.35, -1.53) * mm});
            skLineSegment(sketch, "E356", {"start": v(-14.35, -1.53) * mm, "end": v(-13.96, -1.53) * mm});
            skLineSegment(sketch, "E357", {"start": v(-13.96, -1.53) * mm, "end": v(-13.93, -1.53) * mm});
            skLineSegment(sketch, "E358", {"start": v(-13.93, -1.53) * mm, "end": v(-13.84, -1.43) * mm});
            skLineSegment(sketch, "E359", {"start": v(-13.84, -1.43) * mm, "end": v(-13.84, -1.4) * mm});
            skLineSegment(sketch, "E360", {"start": v(-13.84, -1.4) * mm, "end": v(-13.84, 0.32) * mm});
            skLineSegment(sketch, "E361", {"start": v(-13.84, 0.32) * mm, "end": v(-13.84, 0.32) * mm});
            skLineSegment(sketch, "E362", {"start": v(-13.84, 0.32) * mm, "end": v(-13.8, 0.38) * mm});
            skLineSegment(sketch, "E363", {"start": v(-13.8, 0.38) * mm, "end": v(-13.77, 0.38) * mm});
            skLineSegment(sketch, "E364", {"start": v(-13.77, 0.38) * mm, "end": v(-13.27, 0.38) * mm});
            skLineSegment(sketch, "E365", {"start": v(-13.27, 0.38) * mm, "end": v(-13.25, 0.38) * mm});
            skLineSegment(sketch, "E366", {"start": v(-13.25, 0.38) * mm, "end": v(-13.2, 0.33) * mm});
            skLineSegment(sketch, "E367", {"start": v(-13.2, 0.33) * mm, "end": v(-13.2, 0.32) * mm});
            skLineSegment(sketch, "E368", {"start": v(-13.2, 0.32) * mm, "end": v(-13.2, -1.4) * mm});
            skLineSegment(sketch, "E369", {"start": v(-13.2, -1.4) * mm, "end": v(-13.2, -1.43) * mm});
            skLineSegment(sketch, "E370", {"start": v(-13.2, -1.43) * mm, "end": v(-13.1, -1.53) * mm});
            skLineSegment(sketch, "E371", {"start": v(-13.1, -1.53) * mm, "end": v(-13.08, -1.53) * mm});
            skLineSegment(sketch, "E372", {"start": v(-13.08, -1.53) * mm, "end": v(-12.7, -1.53) * mm});
            skLineSegment(sketch, "E373", {"start": v(-12.7, -1.53) * mm, "end": v(-12.66, -1.53) * mm});
            skLineSegment(sketch, "E374", {"start": v(-12.66, -1.53) * mm, "end": v(-12.57, -1.43) * mm});
            skLineSegment(sketch, "E375", {"start": v(-12.57, -1.43) * mm, "end": v(-12.57, -1.4) * mm});
            skLineSegment(sketch, "E376", {"start": v(-12.57, -1.4) * mm, "end": v(-12.57, 0.89) * mm});
            skLineSegment(sketch, "E377", {"start": v(-12.57, 0.89) * mm, "end": v(-12.57, 0.92) * mm});
            skLineSegment(sketch, "E378", {"start": v(-12.57, 0.92) * mm, "end": v(-12.66, 1.01) * mm});
            skLineSegment(sketch, "E379", {"start": v(-12.66, 1.01) * mm, "end": v(-12.7, 1.01) * mm});
            skLineSegment(sketch, "E380", {"start": v(-11.17, -1.4) * mm, "end": v(-11.17, -1.43) * mm});
            skLineSegment(sketch, "E381", {"start": v(-11.17, -1.43) * mm, "end": v(-11.27, -1.53) * mm});
            skLineSegment(sketch, "E382", {"start": v(-11.27, -1.53) * mm, "end": v(-11.3, -1.53) * mm});
            skLineSegment(sketch, "E383", {"start": v(-11.3, -1.53) * mm, "end": v(-11.68, -1.53) * mm});
            skLineSegment(sketch, "E384", {"start": v(-11.68, -1.53) * mm, "end": v(-11.7, -1.53) * mm});
            skLineSegment(sketch, "E385", {"start": v(-11.7, -1.53) * mm, "end": v(-11.8, -1.43) * mm});
            skLineSegment(sketch, "E386", {"start": v(-11.8, -1.43) * mm, "end": v(-11.8, -1.4) * mm});
            skLineSegment(sketch, "E387", {"start": v(-11.8, -1.4) * mm, "end": v(-11.8, 0.89) * mm});
            skLineSegment(sketch, "E388", {"start": v(-11.8, 0.89) * mm, "end": v(-11.8, 0.92) * mm});
            skLineSegment(sketch, "E389", {"start": v(-11.8, 0.92) * mm, "end": v(-11.7, 1.01) * mm});
            skLineSegment(sketch, "E390", {"start": v(-11.7, 1.01) * mm, "end": v(-11.68, 1.01) * mm});
            skLineSegment(sketch, "E391", {"start": v(-11.68, 1.01) * mm, "end": v(-11.3, 1.01) * mm});
            skLineSegment(sketch, "E392", {"start": v(-11.3, 1.01) * mm, "end": v(-11.27, 1.01) * mm});
            skLineSegment(sketch, "E393", {"start": v(-11.27, 1.01) * mm, "end": v(-11.17, 0.92) * mm});
            skLineSegment(sketch, "E394", {"start": v(-11.17, 0.92) * mm, "end": v(-11.17, 0.89) * mm});
            skLineSegment(sketch, "E395", {"start": v(-11.17, 0.89) * mm, "end": v(-11.17, -1.4) * mm});
            skLineSegment(sketch, "E396", {"start": v(3.52, 0.13) * mm, "end": v(4.02, 0.13) * mm});
            skLineSegment(sketch, "E397", {"start": v(4.02, 0.13) * mm, "end": v(4.05, 0.13) * mm});
            skLineSegment(sketch, "E398", {"start": v(4.05, 0.13) * mm, "end": v(4.15, 0.03) * mm});
            skLineSegment(sketch, "E399", {"start": v(4.15, 0.03) * mm, "end": v(4.15, 0) * mm});
            skLineSegment(sketch, "E400", {"start": v(4.15, 0) * mm, "end": v(4.15, -0.5) * mm});
            skLineSegment(sketch, "E401", {"start": v(4.15, -0.5) * mm, "end": v(4.15, -0.54) * mm});
            skLineSegment(sketch, "E402", {"start": v(4.15, -0.54) * mm, "end": v(4.05, -0.63) * mm});
            skLineSegment(sketch, "E403", {"start": v(4.05, -0.63) * mm, "end": v(4.02, -0.63) * mm});
            skLineSegment(sketch, "E404", {"start": v(4.02, -0.63) * mm, "end": v(3.52, -0.63) * mm});
            skLineSegment(sketch, "E405", {"start": v(3.52, -0.63) * mm, "end": v(3.5, -0.63) * mm});
            skLineSegment(sketch, "E406", {"start": v(3.5, -0.63) * mm, "end": v(3.4, -0.54) * mm});
            skLineSegment(sketch, "E407", {"start": v(3.4, -0.54) * mm, "end": v(3.4, -0.5) * mm});
            skLineSegment(sketch, "E408", {"start": v(3.4, -0.5) * mm, "end": v(3.4, 0) * mm});
            skLineSegment(sketch, "E409", {"start": v(3.4, 0) * mm, "end": v(3.4, 0.03) * mm});
            skLineSegment(sketch, "E410", {"start": v(3.4, 0.03) * mm, "end": v(3.5, 0.13) * mm});
            skLineSegment(sketch, "E411", {"start": v(3.5, 0.13) * mm, "end": v(3.52, 0.13) * mm});
            skSolve(sketch);
        }
        {
            var Q0;
            Q0 = qSketchRegion(id + "F0", true);
            extrude(context, id + "F1", {"entities" : qUnion([Q0]), "oppositeDirection" : true, "depth" : 1.27 * mm});
        }
    });
